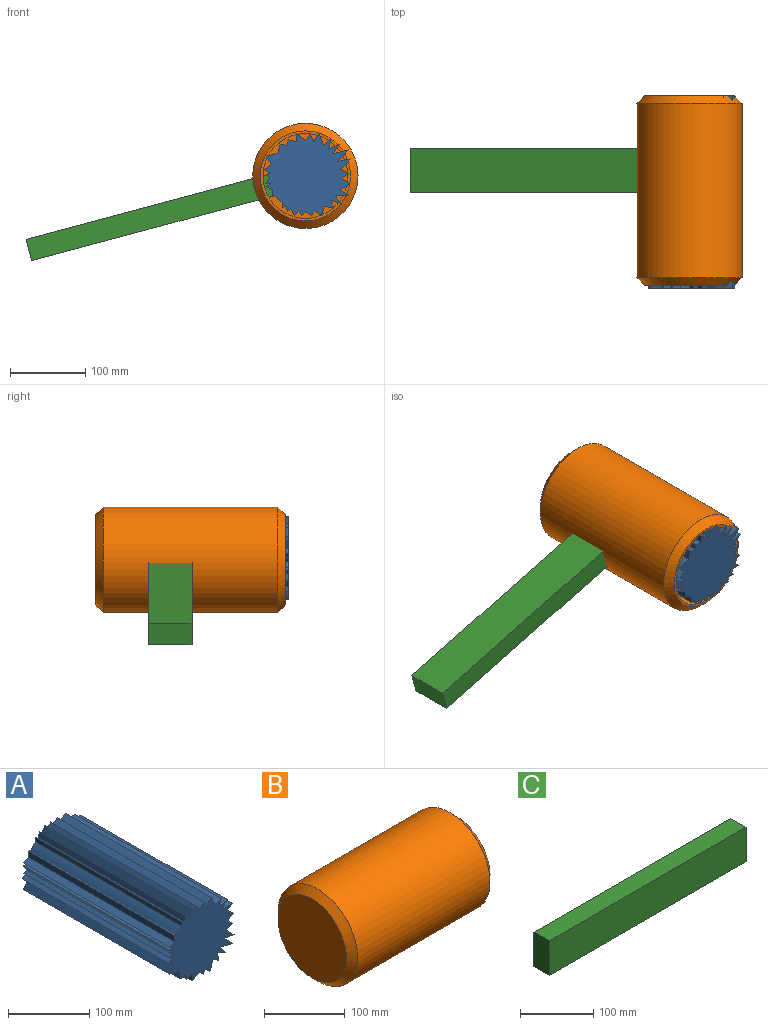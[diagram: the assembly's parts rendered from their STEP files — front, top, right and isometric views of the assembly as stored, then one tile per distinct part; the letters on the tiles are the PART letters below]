
ASSEMBLY  parts=3 mates=2
PART A: 56 faces, bbox 114.3x254.9x109.4 mm
  f0: plane 254.86x8.24mm, normal (-0.84,0,-0.54), area 2504.4mm2, adj f1,f53,f54,f55
  f1: plane 254.86x9.52mm, normal (0.89,0,-0.45), area 2723.5mm2, adj f0,f2,f54,f55
  f2: plane 254.86x10.87mm, normal (-0.84,0,-0.54), area 3302.3mm2, adj f1,f3,f54,f55
  f3: plane 254.86x16.25mm, normal (0.93,0,-0.36), area 4435.4mm2, adj f2,f4,f54,f55
  f4: plane 254.86x9.48mm, normal (-0.65,0,-0.76), area 3183.3mm2, adj f3,f5,f54,f55
  f5: plane 254.86x13.11mm, normal (0.98,0,0.2), area 3407.5mm2, adj f4,f6,f54,f55
  f6: plane 254.86x13.58mm, normal (-0.4,0,-0.91), area 3783.6mm2, adj f5,f7,f54,f55
  f7: plane 254.86x12.02mm, normal (0.84,0,0.54), area 3651.5mm2, adj f6,f8,f54,f55
  f8: plane 254.86x20.38mm, normal (-0.23,0,-0.97), area 5336.2mm2, adj f7,f9,f54,f55
  f9: plane 254.86x14.93mm, normal (0.73,0,0.69), area 5243.7mm2, adj f8,f10,f54,f55
  f10: plane 254.86x16.87mm, normal (-0.18,0,-0.98), area 4367.3mm2, adj f9,f11,f54,f55
  f11: plane 254.86x13.81mm, normal (0.72,0,0.7), area 4918.3mm2, adj f10,f12,f54,f55
  f12: plane 254.86x10.77mm, normal (0.41,0,-0.91), area 3013.4mm2, adj f11,f13,f54,f55
  f13: plane 254.86x10.08mm, normal (0.57,0,0.82), area 3115.1mm2, adj f12,f14,f54,f55
  f14: plane 254.86x11.16mm, normal (0.54,0,-0.84), area 3390.9mm2, adj f13,f15,f54,f55
  f15: plane 254.86x12.52mm, normal (0.55,0,0.84), area 3806.7mm2, adj f14,f16,f54,f55
  f16: plane 254.86x11.71mm, normal (0.54,0,-0.84), area 3557.1mm2, adj f15,f17,f54,f55
  f17: plane 254.86x18.12mm, normal (0,0,1), area 4618.1mm2, adj f16,f18,f54,f55
  f18: plane 254.86x10.45mm, normal (0.77,0,-0.64), area 3455.6mm2, adj f17,f19,f54,f55
  f19: plane 254.86x14.05mm, normal (-0.26,0,0.97), area 3704.8mm2, adj f18,f20,f54,f55
  f20: plane 254.86x10.25mm, normal (0.94,0,-0.34), area 2782.1mm2, adj f19,f21,f54,f55
  f21: plane 254.86x12.81mm, normal (-0.22,0,0.97), area 3349.8mm2, adj f20,f22,f54,f55
  f22: plane 254.86x12.4mm, normal (0.96,0,0.26), area 3275.9mm2, adj f21,f23,f54,f55
  f23: plane 254.86x9.55mm, normal (-0.54,0,0.84), area 2902.5mm2, adj f22,f24,f54,f55
  f24: plane 254.86x6.2mm, normal (0.84,0,0.54), area 1883.1mm2, adj f23,f25,f54,f55
  f25: plane 254.86x8.15mm, normal (-0.54,0,0.84), area 2476.2mm2, adj f24,f26,f54,f55
  f26: plane 254.86x5.29mm, normal (0.78,0,0.63), area 1737.8mm2, adj f25,f27,f54,f55
  f27: plane 254.86x6.2mm, normal (-0.8,0,0.61), area 1986.8mm2, adj f26,f28,f54,f55
  f28: plane 254.86x6.2mm, normal (0.76,0,0.65), area 2076.9mm2, adj f27,f29,f54,f55
  f29: plane 254.86x9.45mm, normal (-0.89,0,0.46), area 2707.6mm2, adj f28,f30,f54,f55
  f30: plane 254.86x4.62mm, normal (0.68,0,0.73), area 1608.2mm2, adj f29,f31,f54,f55
  f31: plane 254.86x8mm, normal (-0.97,0,0.25), area 2108.6mm2, adj f30,f32,f54,f55
  f32: plane 254.86x4.84mm, normal (0.54,0,0.84), area 1468mm2, adj f31,f33,f54,f55
  f33: plane 254.86x6.8mm, normal (-1,0,0), area 1733.3mm2, adj f32,f34,f54,f55
  f34: cylinder r=47.25mm len=254.86mm, axis (0,1,0), area 3210.4mm2, adj f33,f35,f54,f55
  f35: plane 254.86x4.22mm, normal (0.36,0,0.93), area 1150.9mm2, adj f34,f36,f54,f55
  f36: plane 254.86x9.39mm, normal (-1,0,0), area 2393.8mm2, adj f35,f37,f54,f55
  f37: plane 254.86x8.69mm, normal (-0.43,0,0.9), area 2454.9mm2, adj f36,f38,f54,f55
  f38: plane 254.86x6.06mm, normal (-0.55,0,-0.84), area 1848.3mm2, adj f37,f39,f54,f55
  f39: plane 254.86x6.41mm, normal (0,0,1), area 1632.4mm2, adj f38,f40,f54,f55
  f40: plane 254.86x8.8mm, normal (-0.86,0,-0.51), area 2614.5mm2, adj f39,f41,f54,f55
  f41: plane 254.86x4.39mm, normal (-0.59,0,0.81), area 1383.7mm2, adj f40,f42,f54,f55
  f42: plane 254.86x4.5mm, normal (-0.41,0,-0.91), area 1259.4mm2, adj f41,f43,f54,f55
  f43: cylinder r=47.25mm len=254.86mm, axis (0,1,0), area 80.1mm2, adj f42,f44,f54,f55
  f44: plane 254.86x7.24mm, normal (-0.54,0,0.84), area 2198.8mm2, adj f43,f45,f54,f55
  f45: plane 254.86x9.47mm, normal (-0.55,0,-0.84), area 2887.8mm2, adj f44,f46,f54,f55
  f46: plane 254.86x11.11mm, normal (-0.85,0,0.52), area 3315.2mm2, adj f45,f47,f54,f55
  f47: plane 254.86x15.54mm, normal (-0.28,0,-0.96), area 4126.6mm2, adj f46,f48,f54,f55
  f48: plane 254.86x11.76mm, normal (-0.98,0,-0.2), area 3055.3mm2, adj f47,f49,f54,f55
  f49: plane 254.86x9.28mm, normal (0.2,0,-0.98), area 2410.5mm2, adj f48,f50,f54,f55
  f50: plane 254.86x7.32mm, normal (-0.98,0,-0.2), area 1901.2mm2, adj f49,f51,f54,f55
  f51: plane 254.86x10.69mm, normal (0.2,0,-0.98), area 2776.7mm2, adj f50,f52,f54,f55
  f52: plane 254.86x10.08mm, normal (-1,0,0), area 2568.7mm2, adj f51,f53,f54,f55
  f53: plane 254.86x13.02mm, normal (0.54,0,-0.84), area 3956.9mm2, adj f0,f52,f54,f55
  f54: plane 114.26x109.39mm, normal (0,-1,0), area 8385.4mm2, adj f0,f1,f2,f3,f4,f5,f6,f7
  f55: plane 114.26x109.39mm, normal (0,1,0), area 8385.4mm2, adj f0,f1,f2,f3,f4,f5,f6,f7
PART B: 9 faces, bbox 251x139.4x139.4 mm
  f0: cylinder r=69.7mm len=231mm, axis (-1,0,0), area 101165.1mm2, adj f3,f4
  f1: plane 119.4x119.4mm, normal (1,0,0), area 1287mm2, adj f4,f8
  f2: plane 119.4x119.4mm, normal (-1,0,0), area 11197.3mm2, adj f3
  f3: cone r=69.7mm half-angle=45deg, axis (1,0,0), area 5749.2mm2, adj f0,f2
  f4: cone r=59.7mm half-angle=45deg, axis (-1,0,0), area 5749.2mm2, adj f0,f1
  f5: cylinder r=67.2mm len=228.93mm, axis (-1,0,0), area 96662mm2, adj f7,f8
  f6: plane 117.33x117.33mm, normal (1,0,0), area 10812.2mm2, adj f7
  f7: cone r=67.93mm half-angle=45deg, axis (1,0,0), area 4773.2mm2, adj f5,f6
  f8: cone r=57.93mm half-angle=45deg, axis (-1,0,0), area 6048.6mm2, adj f1,f5
PART C: 6 faces, bbox 379.4x29.3x57.8 mm
  f0: plane 379.4x29.27mm, normal (0,0,-1), area 11103.3mm2, adj f1,f2,f3,f4
  f1: plane 379.4x57.8mm, normal (0,1,0), area 21931.1mm2, adj f0,f3,f4,f5
  f2: plane 379.4x57.8mm, normal (0,-1,0), area 21931.1mm2, adj f0,f3,f4,f5
  f3: plane 57.8x29.27mm, normal (-1,0,0), area 1691.7mm2, adj f0,f1,f2,f5
  f4: plane 57.8x29.27mm, normal (1,0,0), area 1691.7mm2, adj f0,f1,f2,f5
  f5: plane 379.4x29.27mm, normal (0,0,1), area 11103.3mm2, adj f1,f2,f3,f4
PLACE A rot(axis=(-1,0,0),180deg) t=(11.22,-160.52,27.96)mm
PLACE B rot(axis=(0.58,-0.58,-0.58),120deg) t=(157.75,-205.65,10226.35)mm
PLACE C rot(axis=(-0.09,0.7,0.7),169.4deg) t=(-71.13,-257.11,45.5)mm
MATE revolute A.f34 <-> C.f0  axis (0,-1,0) through (-64.11,-233.08,19.31)mm
MATE parallel B.f0 <-> A.f34  axis (0,1,0) through (-64.09,-105.65,19.23)mm
